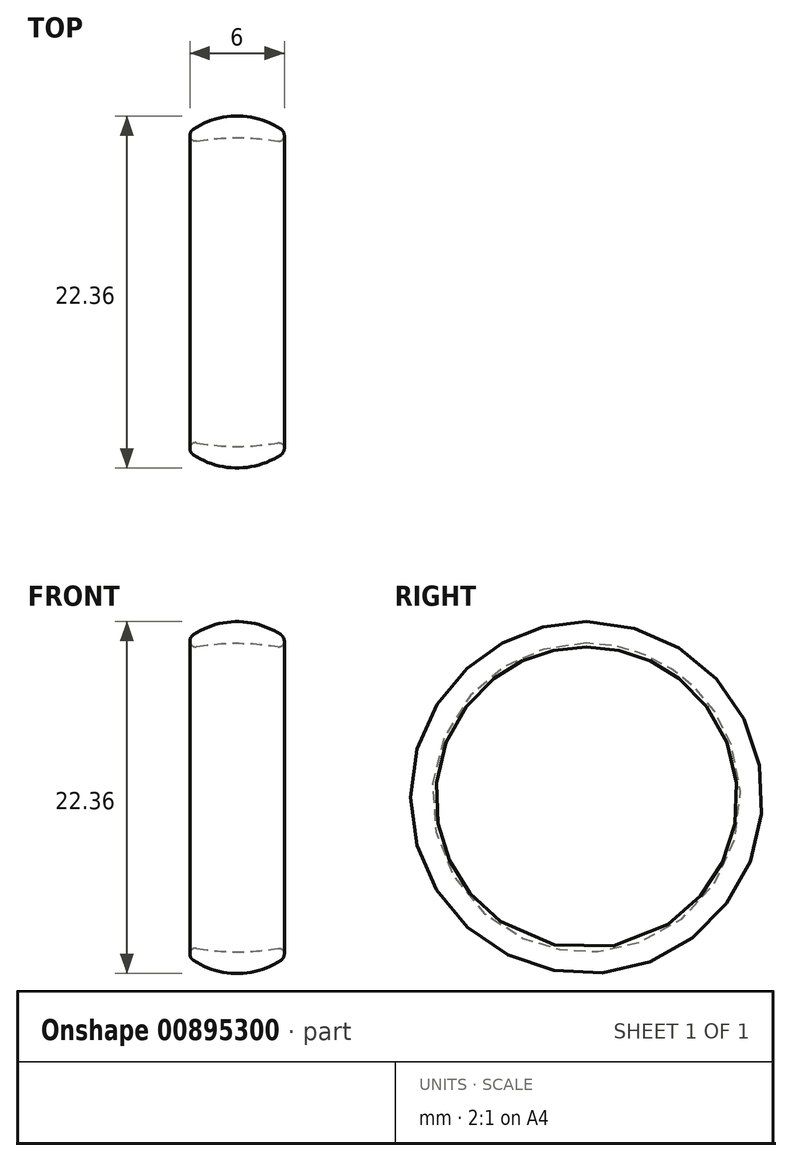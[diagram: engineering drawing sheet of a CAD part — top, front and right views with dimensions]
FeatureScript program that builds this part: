
annotation { "Feature Type Name" : "Feature", "Feature Type Description" : "" }
export const myFeature = defineFeature(function(context is Context, id is Id, definition is map)
    precondition{}
    {
        {
            var Q0;
            Q0=qCreatedBy(makeId("Top.planeOp"),FACE);
            var sketch = newSketch(context, id + "F0", { "sketchPlane" : qUnion([Q0])});
            skLineSegment(sketch, "E0", {"start": v(-2.77, 10.35) * mm, "end": v(-2.77, 10.35) * mm});
            skLineSegment(sketch, "E1", {"start": v(-3, 9.93) * mm, "end": v(-3, 9.93) * mm});
            skLineSegment(sketch, "E2", {"start": v(-2.59, 9.58) * mm, "end": v(-2.59, 9.58) * mm});
            skPoint(sketch, "E3.visualSharp", {"position": v(-3, 9.5) * mm});
            skArc(sketch, "E3.filletArc", {"start": v(-3, 9.93) * mm, "mid": v(-2.87, 9.66) * mm, "end": v(-2.59, 9.58) * mm});
            skPoint(sketch, "E4.visualSharp", {"position": v(-3, 10.2) * mm});
            skArc(sketch, "E4.filletArc", {"start": v(-2.77, 10.35) * mm, "mid": v(-2.94, 10.16) * mm, "end": v(-3, 9.93) * mm});
            skLineSegment(sketch, "E5.MirrorCS", {"start": v(3, 9.93) * mm, "end": v(3, 9.93) * mm});
            skArc(sketch, "E6.MirrorCS", {"start": v(3, 9.93) * mm, "mid": v(2.87, 9.66) * mm, "end": v(2.59, 9.58) * mm});
            skArc(sketch, "E7.MirrorCS", {"start": v(2.77, 10.35) * mm, "mid": v(2.94, 10.16) * mm, "end": v(3, 9.93) * mm});
            skLineSegment(sketch, "E8.MirrorCS", {"start": v(2.77, 10.35) * mm, "end": v(2.77, 10.35) * mm});
            skPoint(sketch, "E9.MirrorP", {"position": v(3, 9.5) * mm});
            skPoint(sketch, "E10.MirrorP", {"position": v(3, 10.2) * mm});
            skLineSegment(sketch, "E11.MirrorCS", {"start": v(2.59, 9.58) * mm, "end": v(2.59, 9.58) * mm});
            skPoint(sketch, "E12.visualSharp", {"position": v(0, 12.17) * mm});
            skArc(sketch, "E12.filletArc", {"start": v(2.77, 10.35) * mm, "mid": v(0, 11.18) * mm, "end": v(-2.77, 10.35) * mm});
            skPoint(sketch, "E13.visualSharp", {"position": v(0, 10.03) * mm});
            skArc(sketch, "E13.filletArc", {"start": v(2.59, 9.58) * mm, "mid": v(0, 9.8) * mm, "end": v(-2.59, 9.58) * mm});
            skLineSegment(sketch, "E14", {"start": v(0, 0) * mm, "end": v(4.65, 0) * mm, "construction": true});
            skLineSegment(sketch, "E15", {"start": v(3.05, 9.57) * mm, "end": v(4.75, 9.57) * mm, "construction": true});
            skSolve(sketch);
        }
        {
            var Q0;
            Q0=makeQuery(id+"F0.imprint","IMPRINT",FACE,{"disambiguationData":[TD([[makeQuery(id+"F0.imprint","IMPRINT",EDGE,{"derivedFrom":sQuery(id+"F0.wireOp",EDGE,"E1")}),1.0]])]});
            var Q1;
            Q1=makeQuery(id+"F0.imprint","IMPRINT",FACE,{"disambiguationData":[TD([[makeQuery(id+"F0.imprint","IMPRINT",EDGE,{"derivedFrom":sQuery(id+"F0.wireOp",EDGE,"E3.filletArc")}),1.0]])]});
            var Q2;
            Q2=sQuery(id+"F0.wireOp",EDGE,"E14");
            revolve(context, id + "F1", {"surfaceOperationType" : NewSurfaceOperationType.NEW, "entities" : qUnion([Q0, Q1]), "axis" : qUnion([Q2]), "revolveType" : RevolveType.FULL});
        }
    });
